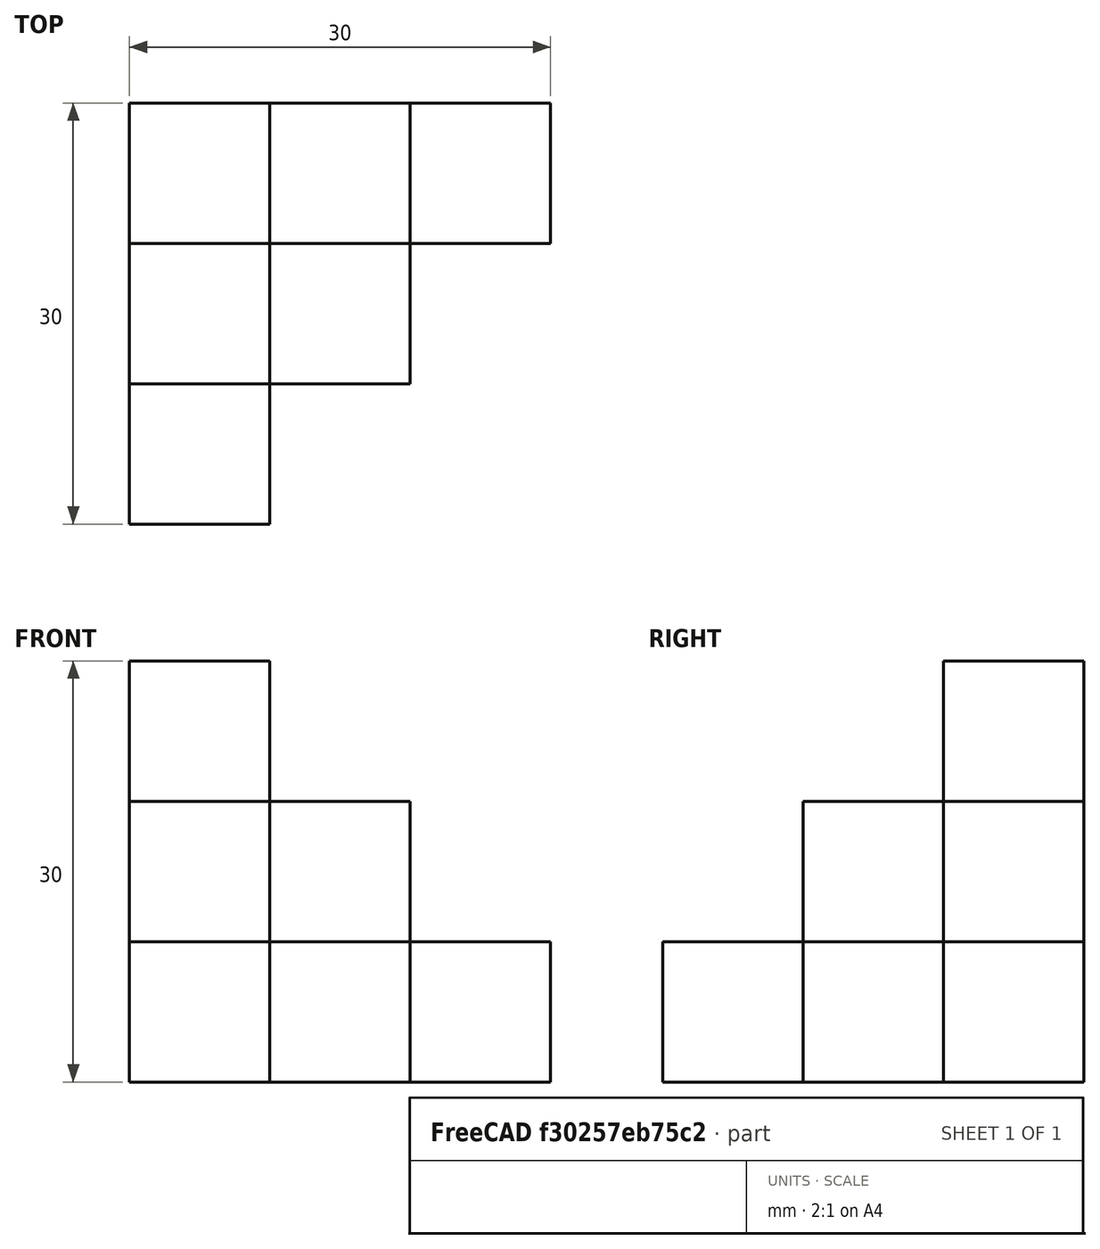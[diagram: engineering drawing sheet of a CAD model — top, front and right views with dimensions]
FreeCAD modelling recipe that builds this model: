
FCSTD DOCUMENT  (FreeCAD 0.21R33694 (Git))
Label: OJT1_T04_R02
License: All rights reserved
LicenseURL: https://en.wikipedia.org/wiki/All_rights_reserved
objects: Part::Box×6
note: 6 computed .brp shape members not serialized (recipe doc carries the construction recipe); baked Part::Feature solids carry a one-line shape summary decoded from their .brp

FEATURE [Part::Box] Box  label="Nivell2-Cub1"
  AttacherType = Attacher::AttachEngine3D
  Height = 20
  Length = 10
  Width = 10
FEATURE [Part::Box] Box001  label="Nivell1-Cub2"
  AttacherType = Attacher::AttachEngine3D
  Height = 10
  Length = 10
  Placement = pos=(10,0,0) rot=(0,0,1;0rad)
  Width = 10
FEATURE [Part::Box] Box002  label="Nivell1-Cub1"
  AttacherType = Attacher::AttachEngine3D
  Height = 10
  Length = 10
  Placement = pos=(0,-10,0) rot=(0,0,1;0rad)
  Width = 10
FEATURE [Part::Box] Box003  label="Nivell2-Cub003"
  AttacherType = Attacher::AttachEngine3D
  Height = 20
  Length = 10
  Placement = pos=(10,10,0) rot=(0,0,1;0rad)
  Width = 10
FEATURE [Part::Box] Box004  label="Nivell1-Cub3"
  AttacherType = Attacher::AttachEngine3D
  Height = 10
  Length = 10
  Placement = pos=(20,10,0) rot=(0,0,1;0rad)
  Width = 10
FEATURE [Part::Box] Box005  label="Nivell3_Cub1"
  AttacherType = Attacher::AttachEngine3D
  Height = 30
  Length = 10
  Placement = pos=(0,10,0) rot=(0,0,1;0rad)
  Width = 10
